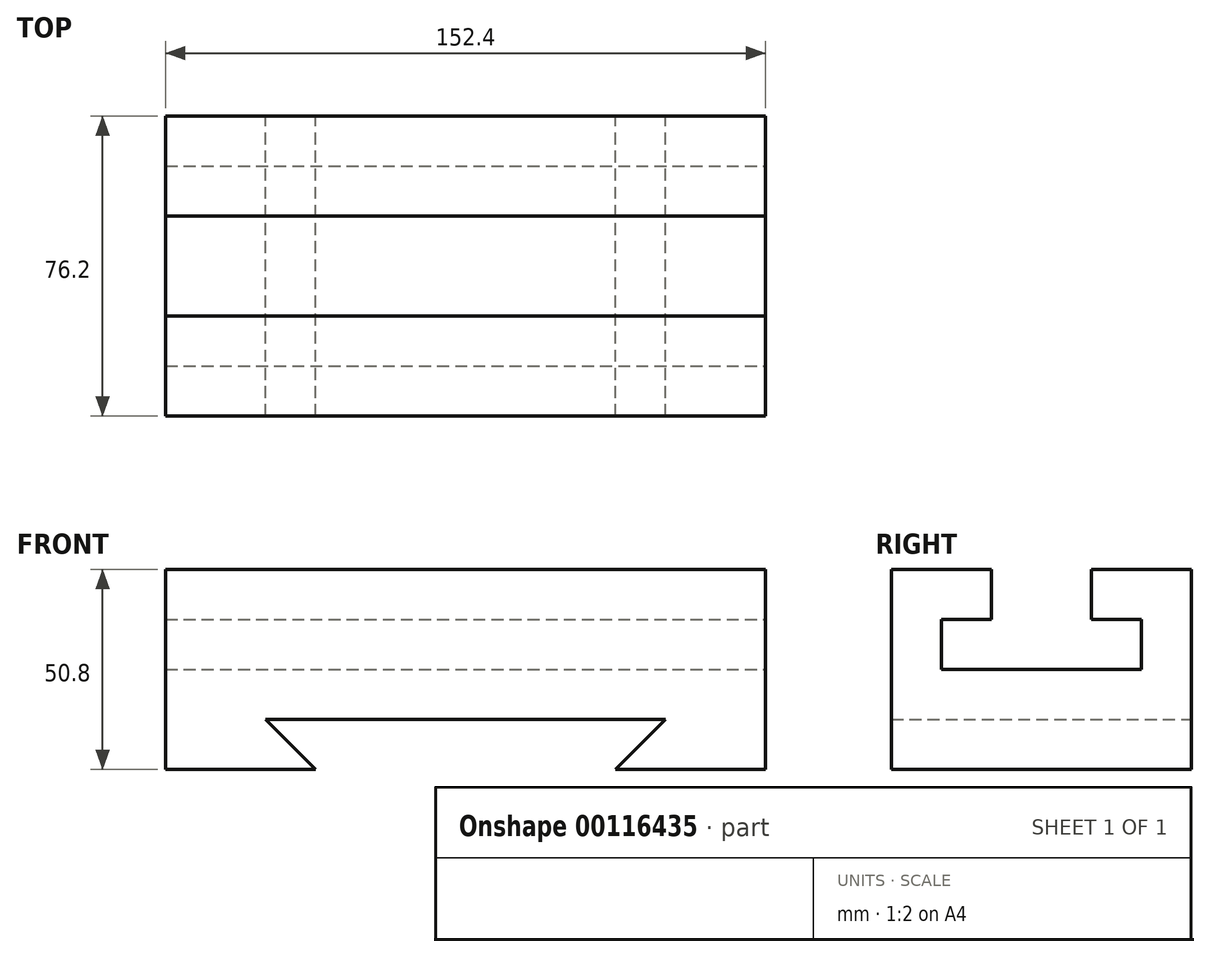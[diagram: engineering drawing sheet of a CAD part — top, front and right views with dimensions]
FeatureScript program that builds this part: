
annotation { "Feature Type Name" : "Feature", "Feature Type Description" : "" }
export const myFeature = defineFeature(function(context is Context, id is Id, definition is map)
    precondition{}
    {
        {
            var Q0;
            Q0=qCreatedBy(makeId("Front.planeOp"),FACE);
            var sketch = newSketch(context, id + "F0", { "sketchPlane" : qUnion([Q0])});
            skLineSegment(sketch, "E0", {"start": v(0, 0) * mm, "end": v(101.6, 0) * mm});
            skLineSegment(sketch, "E1", {"start": v(12.7, -12.7) * mm, "end": v(0, 0) * mm});
            skLineSegment(sketch, "E2", {"start": v(12.7, -12.7) * mm, "end": v(-25.4, -12.7) * mm});
            skLineSegment(sketch, "E3", {"start": v(-25.4, -12.7) * mm, "end": v(-25.4, 38.1) * mm});
            skLineSegment(sketch, "E4", {"start": v(-25.4, 38.1) * mm, "end": v(127, 38.1) * mm});
            skLineSegment(sketch, "E5", {"start": v(127, 38.1) * mm, "end": v(127, -12.7) * mm});
            skLineSegment(sketch, "E6", {"start": v(127, -12.7) * mm, "end": v(88.9, -12.7) * mm});
            skLineSegment(sketch, "E7", {"start": v(101.6, 0) * mm, "end": v(88.9, -12.7) * mm});
            skSolve(sketch);
        }
        {
            var Q0;
            Q0=makeQuery(id+"F0.imprint","IMPRINT",FACE,{"disambiguationData":[TD([[makeQuery(id+"F0.imprint","IMPRINT",EDGE,{"derivedFrom":sQuery(id+"F0.wireOp",EDGE,"E0")}),1.0]])]});
            extrude(context, id + "F1", {"entities" : qUnion([Q0]), "depth" : 76.2 * mm});
        }
        {
            var Q0;
            Q0=makeQuery(id+"F1.opExtrude","SWEPT_FACE",FACE,{"disambiguationData":[OSD([sQuery(id+"F0.wireOp",EDGE,"E5")])]});
            var sketch = newSketch(context, id + "F2", { "sketchPlane" : qUnion([Q0])});
            skLineSegment(sketch, "E8", {"start": v(-50.8, 38.1) * mm, "end": v(-50.8, 12.7) * mm});
            skLineSegment(sketch, "E9", {"start": v(-50.8, 12.7) * mm, "end": v(-25.4, 12.7) * mm});
            skLineSegment(sketch, "E10", {"start": v(-25.4, 12.7) * mm, "end": v(-25.4, 38.1) * mm});
            skLineSegment(sketch, "E11", {"start": v(-25.4, 38.1) * mm, "end": v(-50.8, 38.1) * mm});
            skSolve(sketch);
        }
        {
            var Q0;
            Q0=makeQuery(id+"F2.imprint","IMPRINT",FACE,{"disambiguationData":[TD([[makeQuery(id+"F2.imprint","IMPRINT",EDGE,{"derivedFrom":sQuery(id+"F2.wireOp",EDGE,"E8")}),1.0]])]});
            extrude(context, id + "F3", {"entities" : qUnion([Q0]), "operationType" : NewBodyOperationType.REMOVE, "endBound" : BoundingType.THROUGH_ALL, "oppositeDirection" : true, "depth" : 25.4 * mm});
        }
        {
            var Q0;
            Q0=makeQuery(id+"F1.opExtrude","SWEPT_FACE",FACE,{"disambiguationData":[OSD([sQuery(id+"F0.wireOp",EDGE,"E5")])]});
            var sketch = newSketch(context, id + "F4", { "sketchPlane" : qUnion([Q0])});
            skLineSegment(sketch, "E12", {"start": v(-50.8, 25.4) * mm, "end": v(-63.5, 25.4) * mm});
            skLineSegment(sketch, "E13", {"start": v(-63.5, 25.4) * mm, "end": v(-63.5, 12.7) * mm});
            skLineSegment(sketch, "E14", {"start": v(-63.5, 12.7) * mm, "end": v(-12.7, 12.7) * mm});
            skLineSegment(sketch, "E15", {"start": v(-12.7, 12.7) * mm, "end": v(-12.7, 25.4) * mm});
            skLineSegment(sketch, "E16", {"start": v(-12.7, 25.4) * mm, "end": v(-50.8, 25.4) * mm});
            skSolve(sketch);
        }
        {
            var Q0;
            {var subQ3=sQuery(id+"F4.wireOp",EDGE,"E15");Q0=makeQuery(id+"F4.imprint","IMPRINT",FACE,{"disambiguationData":[TD([[makeQuery(id+"F4.imprint","IMPRINT",EDGE,{"derivedFrom":subQ3}),1.0]])]});}
            var Q1;
            {var subQ0=sQuery(id+"F4.wireOp",EDGE,"E12");Q1=makeQuery(id+"F4.imprint","IMPRINT",FACE,{"disambiguationData":[TD([[makeQuery(id+"F4.imprint","IMPRINT",EDGE,{"derivedFrom":subQ0}),1.0]])]});}
            extrude(context, id + "F5", {"entities" : qUnion([Q0, Q1]), "operationType" : NewBodyOperationType.REMOVE, "endBound" : BoundingType.THROUGH_ALL, "oppositeDirection" : true, "depth" : 25.4 * mm});
        }
    });
